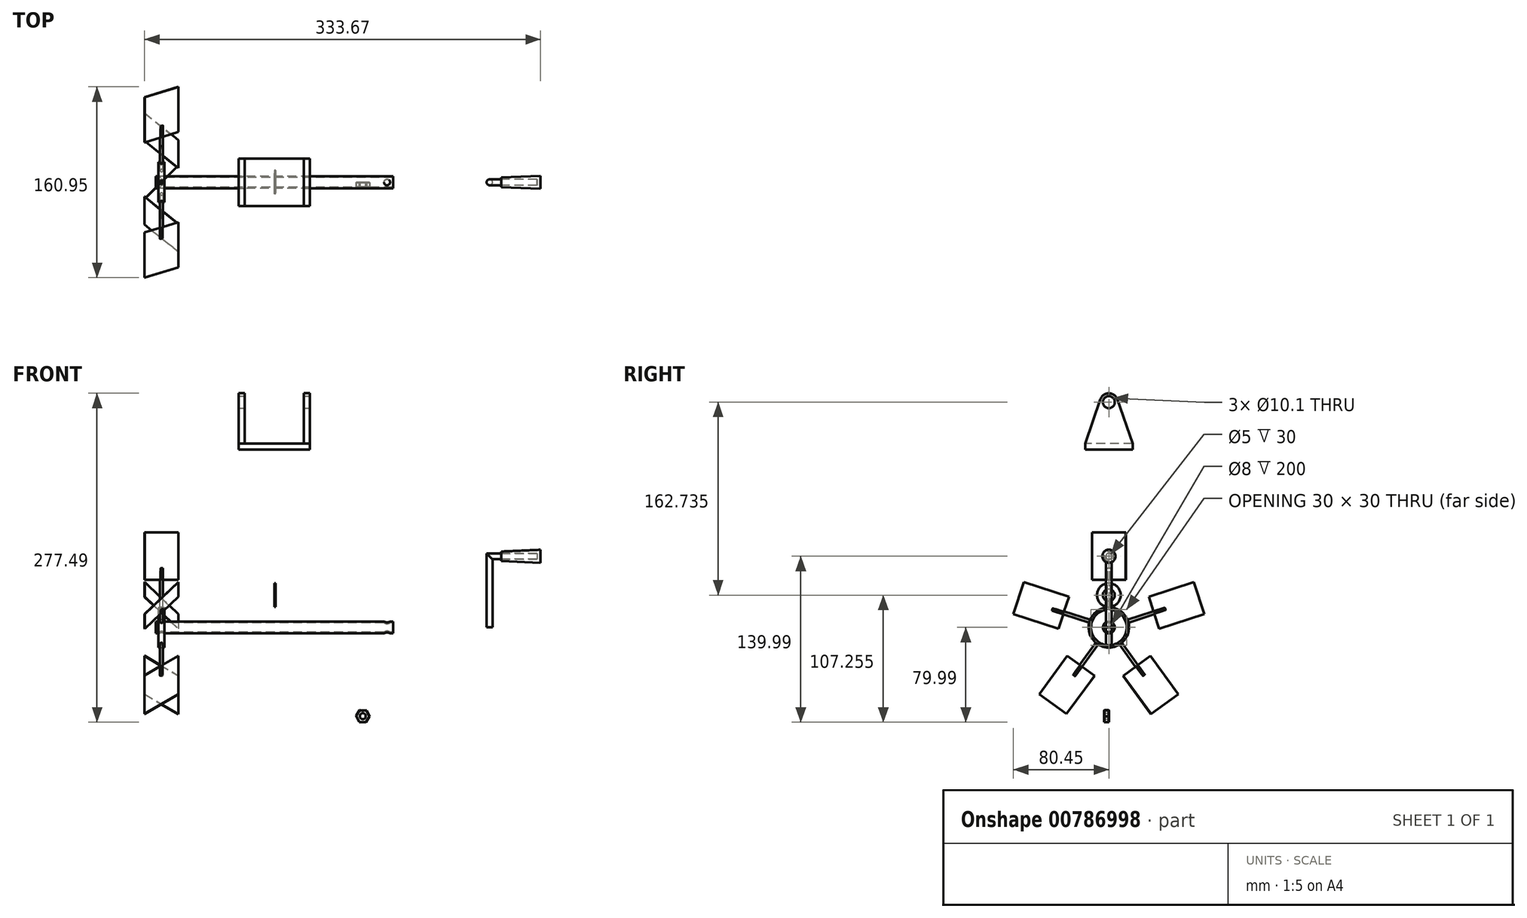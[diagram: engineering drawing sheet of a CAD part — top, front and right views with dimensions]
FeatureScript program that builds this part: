
annotation { "Feature Type Name" : "Feature", "Feature Type Description" : "" }
export const myFeature = defineFeature(function(context is Context, id is Id, definition is map)
    precondition{}
    {
        {
            var Q0;
            Q0=qCreatedBy(makeId("Front.planeOp"),FACE);
            var sketch = newSketch(context, id + "F0", { "sketchPlane" : qUnion([Q0])});
            skLineSegment(sketch, "E0.bottom", {"start": v(-100, 5) * mm, "end": v(100, 5) * mm});
            skLineSegment(sketch, "E0.top", {"start": v(-100, 4) * mm, "end": v(100, 4) * mm});
            skLineSegment(sketch, "E0.left", {"start": v(-100, 5) * mm, "end": v(-100, 4) * mm});
            skLineSegment(sketch, "E0.right", {"start": v(100, 5) * mm, "end": v(100, 4) * mm});
            skLineSegment(sketch, "E1", {"start": v(-144.44, 0) * mm, "end": v(183.91, 0) * mm, "construction": true});
            skSolve(sketch);
        }
        {
            var Q0;
            Q0 = qSketchRegion(id + "F0", true);
            var Q1;
            Q1=sQuery(id+"F0.wireOp",EDGE,"E1");
            revolve(context, id + "F1", {"surfaceOperationType" : NewSurfaceOperationType.NEW, "entities" : qUnion([Q0]), "axis" : qUnion([Q1]), "revolveType" : RevolveType.FULL});
        }
        {
            var Q0;
            Q0=qCreatedBy(makeId("Top.planeOp"),FACE);
            cPlane(context, id + "F2", {"entities" : qUnion([Q0]), "cplaneType" : CPlaneType.OFFSET, "offset" : 150 * mm, "width" : 150 * mm, "height" : 150 * mm});
        }
        {
            var Q0;
            Q0=qCreatedBy(id+"F2.planeOp",FACE);
            var sketch = newSketch(context, id + "F3", { "sketchPlane" : qUnion([Q0])});
            skLineSegment(sketch, "E2.bottom", {"start": v(25, 20) * mm, "end": v(-25, 20) * mm});
            skLineSegment(sketch, "E2.top", {"start": v(25, -20) * mm, "end": v(-25, -20) * mm});
            skLineSegment(sketch, "E2.left", {"start": v(25, 20) * mm, "end": v(25, -20) * mm});
            skLineSegment(sketch, "E2.right", {"start": v(-25, 20) * mm, "end": v(-25, -20) * mm});
            skPoint(sketch, "E2.middle", {"position": v(0, 0) * mm});
            skSolve(sketch);
        }
        {
            var Q0;
            Q0 = qSketchRegion(id + "F3", true);
            extrude(context, id + "F4", {"entities" : qUnion([Q0]), "depth" : 5 * mm, "offsetDistance" : 25 * mm});
        }
        {
            var Q0;
            Q0=makeQuery(id+"F4.opExtrude","SWEPT_FACE",FACE,{"disambiguationData":[OSD([sQuery(id+"F3.wireOp",EDGE,"E2.left")])]});
            cPlane(context, id + "F5", {"entities" : qUnion([Q0]), "cplaneType" : CPlaneType.OFFSET, "offset" : 5 * mm, "width" : 150 * mm, "height" : 150 * mm});
        }
        {
            var Q0;
            Q0=qCreatedBy(id+"F5.planeOp",FACE);
            var sketch = newSketch(context, id + "F6", { "sketchPlane" : qUnion([Q0])});
            skLineSegment(sketch, "E3.0", {"start": v(20, 150) * mm, "end": v(-20, 150) * mm});
            skLineSegment(sketch, "E4.0", {"start": v(-20, 155) * mm, "end": v(-20, 150) * mm});
            skLineSegment(sketch, "E5.0", {"start": v(20, 155) * mm, "end": v(20, 150) * mm});
            skCircle(sketch, "E6", {"center": v(0, 190) * mm, "radius": 5.05 * mm});
            skCircle(sketch, "E7", {"center": v(0, 190) * mm, "radius": 7.5 * mm});
            skLineSegment(sketch, "E8", {"start": v(-20, 155) * mm, "end": v(-7.1, 192.44) * mm});
            skLineSegment(sketch, "E9", {"start": v(20, 155) * mm, "end": v(7.1, 192.44) * mm});
            skSolve(sketch);
        }
        {
            var Q0;
            Q0 = qSketchRegion(id + "F6", true);
            extrude(context, id + "F7", {"entities" : qUnion([Q0]), "operationType" : NewBodyOperationType.ADD, "oppositeDirection" : true, "depth" : 5 * mm, "offsetDistance" : 25 * mm});
        }
        {
            var Q0;
            Q0=makeQuery(id+"F4.opExtrude","SWEPT_FACE",FACE,{"disambiguationData":[OSD([sQuery(id+"F3.wireOp",EDGE,"E2.right")])]});
            var sketch = newSketch(context, id + "F8", { "sketchPlane" : qUnion([Q0])});
            skLineSegment(sketch, "E10.0", {"start": v(20, 150) * mm, "end": v(-20, 150) * mm});
            skLineSegment(sketch, "E11.0", {"start": v(-20, 155) * mm, "end": v(-20, 150) * mm});
            skLineSegment(sketch, "E12.0", {"start": v(20, 155) * mm, "end": v(20, 150) * mm});
            skCircle(sketch, "E13", {"center": v(0, 190) * mm, "radius": 5.05 * mm});
            skCircle(sketch, "E14", {"center": v(0, 190) * mm, "radius": 7.5 * mm});
            skLineSegment(sketch, "E15", {"start": v(-20, 155) * mm, "end": v(-7.1, 192.44) * mm});
            skLineSegment(sketch, "E16", {"start": v(20, 155) * mm, "end": v(7.1, 192.44) * mm});
            skSolve(sketch);
        }
        {
            var Q0;
            Q0 = qSketchRegion(id + "F8", true);
            extrude(context, id + "F9", {"entities" : qUnion([Q0]), "operationType" : NewBodyOperationType.ADD, "depth" : 5 * mm, "offsetDistance" : 25 * mm});
        }
        {
            var Q0;
            Q0=qCreatedBy(makeId("Right.planeOp"),FACE);
            var sketch = newSketch(context, id + "F10", { "sketchPlane" : qUnion([Q0])});
            skCircle(sketch, "E17", {"center": v(0, 27.26) * mm, "radius": 5.05 * mm});
            skCircle(sketch, "E18", {"center": v(0, 27.26) * mm, "radius": 10 * mm});
            skSolve(sketch);
        }
        {
            var Q0;
            Q0=makeQuery(id+"F10.imprint","IMPRINT",FACE,{"disambiguationData":[TD([[makeQuery(id+"F10.imprint","IMPRINT",EDGE,{"derivedFrom":sQuery(id+"F10.wireOp",EDGE,"E17")}),-1.0]])]});
            extrude(context, id + "F11", {"entities" : qUnion([Q0]), "depth" : 1 * mm, "offsetDistance" : 25 * mm});
        }
        {
            var Q0;
            Q0=qCreatedBy(makeId("Front.planeOp"),FACE);
            var sketch = newSketch(context, id + "F12", { "sketchPlane" : qUnion([Q0])});
            skLineSegment(sketch, "E19", {"start": v(-100, 5) * mm, "end": v(100, 5) * mm, "construction": true});
            skSolve(sketch);
        }
        {
            var Q0;
            Q0=sQuery(id+"F12.wireOp",EDGE,"E19");
            cPlane(context, id + "F13", {"entities" : qUnion([Q0]), "cplaneType" : CPlaneType.LINE_ANGLE, "offset" : 25 * mm, "angle" : 90 * degree, "width" : 150 * mm, "height" : 150 * mm});
        }
        {
            var Q0;
            Q0=qCreatedBy(id+"F13.planeOp",FACE);
            var sketch = newSketch(context, id + "F14", { "sketchPlane" : qUnion([Q0])});
            skCircle(sketch, "E20", {"center": v(95, 0) * mm, "radius": 2.55 * mm});
            skSolve(sketch);
        }
        {
            var Q0;
            Q0=makeQuery(id+"F14.imprint","IMPRINT",FACE,{"disambiguationData":[TD([[makeQuery(id+"F14.imprint","IMPRINT",EDGE,{"derivedFrom":sQuery(id+"F14.wireOp",EDGE,"E20")}),1.0]])]});
            extrude(context, id + "F15", {"entities" : qUnion([Q0]), "operationType" : NewBodyOperationType.REMOVE, "oppositeDirection" : true, "depth" : 25 * mm, "offsetDistance" : 25 * mm});
        }
        {
            var Q0;
            Q0=qCreatedBy(makeId("Front.planeOp"),FACE);
            var sketch = newSketch(context, id + "F16", { "sketchPlane" : qUnion([Q0])});
            skLineSegment(sketch, "E21", {"start": v(181.39, 0) * mm, "end": v(181.39, 60) * mm});
            skLineSegment(sketch, "E22", {"start": v(181.39, 60) * mm, "end": v(221.39, 60) * mm});
            skSolve(sketch);
        }
        {
            var Q0;
            Q0=qCreatedBy(makeId("Top.planeOp"),FACE);
            var sketch = newSketch(context, id + "F17", { "sketchPlane" : qUnion([Q0])});
            skPoint(sketch, "E23.0", {"position": v(181.39, 0) * mm});
            skCircle(sketch, "E24", {"center": v(181.39, 0) * mm, "radius": 2.5 * mm});
            skSolve(sketch);
        }
        {
            var Q0;
            Q0=makeQuery(id+"F17.imprint","IMPRINT",FACE,{"disambiguationData":[TD([[makeQuery(id+"F17.imprint","IMPRINT",EDGE,{"derivedFrom":sQuery(id+"F17.wireOp",EDGE,"E24")}),1.0]])]});
            var Q1;
            Q1=sQuery(id+"F16.wireOp",EDGE,"E21");
            var Q2;
            Q2=sQuery(id+"F16.wireOp",EDGE,"E22");
            sweep(context, id + "F18", {"profiles" : qUnion([Q0]), "path" : qUnion([Q1, Q2])});
        }
        {
            var Q0;
            Q0=sQuery(id+"F16.wireOp",EDGE,"E22");
            cPlane(context, id + "F19", {"entities" : qUnion([Q0]), "cplaneType" : CPlaneType.LINE_ANGLE, "offset" : 25 * mm, "angle" : 270 * degree, "width" : 150 * mm, "height" : 150 * mm});
        }
        {
            var Q0;
            Q0=qCreatedBy(id+"F19.planeOp",FACE);
            var sketch = newSketch(context, id + "F20", { "sketchPlane" : qUnion([Q0])});
            skLineSegment(sketch, "E25.0", {"start": v(181.39, 0) * mm, "end": v(221.39, 0) * mm});
            skLineSegment(sketch, "E26", {"start": v(224.39, 0) * mm, "end": v(224.39, 5.5) * mm});
            skLineSegment(sketch, "E27", {"start": v(224.39, 5.5) * mm, "end": v(191.39, 4) * mm});
            skLineSegment(sketch, "E28", {"start": v(191.39, 4) * mm, "end": v(191.39, 2.5) * mm});
            skLineSegment(sketch, "E29", {"start": v(191.39, 2.5) * mm, "end": v(221.39, 2.5) * mm});
            skLineSegment(sketch, "E30", {"start": v(221.39, 2.5) * mm, "end": v(221.39, 0) * mm});
            skLineSegment(sketch, "E31", {"start": v(221.39, 0) * mm, "end": v(224.39, 0) * mm});
            skSolve(sketch);
        }
        {
            var Q0;
            Q0=makeQuery(id+"F20.imprint","IMPRINT",FACE,{"disambiguationData":[TD([[makeQuery(id+"F20.imprint","IMPRINT",EDGE,{"derivedFrom":sQuery(id+"F20.wireOp",EDGE,"E26")}),1.0]])]});
            var Q1;
            Q1=sQuery(id+"F20.wireOp",EDGE,"E25.0");
            revolve(context, id + "F21", {"surfaceOperationType" : NewSurfaceOperationType.NEW, "entities" : qUnion([Q0]), "axis" : qUnion([Q1]), "revolveType" : RevolveType.FULL});
        }
        {
            var Q0;
            Q0=qCreatedBy(makeId("Right.planeOp"),FACE);
            cPlane(context, id + "F22", {"entities" : qUnion([Q0]), "cplaneType" : CPlaneType.OFFSET, "offset" : 95 * mm, "oppositeDirection" : true, "width" : 150 * mm, "height" : 150 * mm});
        }
        {
            var Q0;
            Q0=qCreatedBy(id+"F22.planeOp",FACE);
            var sketch = newSketch(context, id + "F23", { "sketchPlane" : qUnion([Q0])});
            skCircle(sketch, "E32", {"center": v(0, 0) * mm, "radius": 15 * mm});
            skCircle(sketch, "E33", {"center": v(0, 0) * mm, "radius": 17 * mm});
            skCircle(sketch, "E34", {"center": v(0, 0) * mm, "radius": 50 * mm, "construction": true});
            skPoint(sketch, "E35", {"position": v(0, 50) * mm});
            skSolve(sketch);
        }
        {
            var Q0;
            Q0 = qSketchRegion(id + "F23", true);
            extrude(context, id + "F24", {"entities" : qUnion([Q0]), "endBound" : BoundingType.SYMMETRIC, "oppositeDirection" : true, "depth" : 5 * mm, "offsetDistance" : 25 * mm});
        }
        {
            var Q0;
            Q0=qCreatedBy(makeId("Top.planeOp"),FACE);
            var sketch = newSketch(context, id + "F25", { "sketchPlane" : qUnion([Q0])});
            skCircle(sketch, "E36", {"center": v(-95, 0) * mm, "radius": 2.5 * mm});
            skSolve(sketch);
        }
        {
            var Q0;
            Q0 = qSketchRegion(id + "F25", true);
            extrude(context, id + "F26", {"entities" : qUnion([Q0]), "operationType" : NewBodyOperationType.ADD, "endBound" : BoundingType.SYMMETRIC, "depth" : 30 * mm, "offsetDistance" : 25 * mm});
        }
        {
            var Q0;
            Q0=sQuery(id+"F23.wireOp",VERTEX,"E35");
            var Q1;
            Q1=qCreatedBy(makeId("Top.planeOp"),FACE);
            cPlane(context, id + "F27", {"entities" : qUnion([Q0, Q1]), "cplaneType" : CPlaneType.PLANE_POINT, "offset" : 25 * mm, "width" : 150 * mm, "height" : 150 * mm});
        }
        {
            var Q0;
            Q0=qCreatedBy(id+"F27.planeOp",FACE);
            var sketch = newSketch(context, id + "F28", { "sketchPlane" : qUnion([Q0])});
            skPoint(sketch, "E37.0", {"position": v(-95, 0) * mm});
            skCircle(sketch, "E38", {"center": v(-95, 0) * mm, "radius": 1.25 * mm});
            skSolve(sketch);
        }
        {
            var Q0;
            Q0 = qSketchRegion(id + "F28", true);
            var Q1;
            Q1=makeQuery(id+"F24.opExtrude","SWEPT_FACE",FACE,{"disambiguationData":[OSD([sQuery(id+"F23.wireOp",EDGE,"E33")])]});
            extrude(context, id + "F29", {"entities" : qUnion([Q0]), "endBound" : BoundingType.UP_TO_SURFACE, "oppositeDirection" : true, "depth" : 25 * mm, "endBoundEntityFace" : qUnion([Q1]), "offsetDistance" : 25 * mm});
        }
        {
            var Q0;
            Q0=makeQuery(id+"F28.imprint","IMPRINT",FACE,{"disambiguationData":[TD([[makeQuery(id+"F28.imprint","IMPRINT",EDGE,{"derivedFrom":sQuery(id+"F28.wireOp",EDGE,"E38")}),1.0]])]});
            var sketch = newSketch(context, id + "F30", { "sketchPlane" : qUnion([Q0])});
            skPoint(sketch, "E39.0", {"position": v(-95, 0) * mm});
            skLineSegment(sketch, "E40", {"start": v(-95, 2.52) * mm, "end": v(-95, -2.49) * mm, "construction": true});
            skCircle(sketch, "E41.0", {"center": v(-95, 0) * mm, "radius": 1.25 * mm});
            skLineSegment(sketch, "E42", {"start": v(-94.27, 1.01) * mm, "end": v(-96.01, -0.73) * mm});
            skLineSegment(sketch, "E43", {"start": v(-95.73, -1.01) * mm, "end": v(-93.99, 0.73) * mm});
            skSolve(sketch);
        }
        {
            var Q0;
            {var subQ0=sQuery(id+"F30.wireOp",EDGE,"E42");Q0=makeQuery(id+"F30.imprint","IMPRINT",FACE,{"disambiguationData":[TD([[makeQuery(id+"F30.imprint","IMPRINT",EDGE,{"derivedFrom":subQ0}),1.0]])]});}
            extrude(context, id + "F31", {"entities" : qUnion([Q0]), "operationType" : NewBodyOperationType.REMOVE, "oppositeDirection" : true, "depth" : 10 * mm, "offsetDistance" : 25 * mm});
        }
        {
            var Q0;
            Q0=makeQuery(id+"F31.boolean.opBoolean","COPY",FACE,{"derivedFrom":makeQuery(id+"F31.opExtrude","SWEPT_FACE",FACE,{"disambiguationData":[OSD([sQuery(id+"F30.wireOp",EDGE,"E42")])]})});
            var sketch = newSketch(context, id + "F32", { "sketchPlane" : qUnion([Q0])});
            skPoint(sketch, "E44.0", {"position": v(-67.18, 50) * mm});
            skLineSegment(sketch, "E45.bottom", {"start": v(-87.18, 80) * mm, "end": v(-47.18, 80) * mm});
            skLineSegment(sketch, "E45.top", {"start": v(-87.18, 40) * mm, "end": v(-47.18, 40) * mm});
            skLineSegment(sketch, "E45.left", {"start": v(-87.18, 80) * mm, "end": v(-87.18, 40) * mm});
            skLineSegment(sketch, "E45.right", {"start": v(-47.18, 80) * mm, "end": v(-47.18, 40) * mm});
            skSolve(sketch);
        }
        {
            var Q0;
            Q0 = qSketchRegion(id + "F32", true);
            extrude(context, id + "F33", {"entities" : qUnion([Q0]), "depth" : 0.2 * mm, "offsetDistance" : 25 * mm});
        }
        {
            var Q0;
            Q0=makeQuery(id+"F29.opExtrude","SWEPT_BODY",BODY,{"disambiguationData":[OSD([sQuery(id+"F28.wireOp",EDGE,"E38")])]});
            var Q1;
            Q1=makeQuery(id+"F33.opExtrude","SWEPT_BODY",BODY,{"disambiguationData":[OSD([sQuery(id+"F32.wireOp",EDGE,"E45.bottom"),sQuery(id+"F32.wireOp",EDGE,"E45.top"),sQuery(id+"F32.wireOp",EDGE,"E45.left"),sQuery(id+"F32.wireOp",EDGE,"E45.right")])]});
            var Q2;
            Q2=sQuery(id+"F23.wireOp",EDGE,"E33");
            circularPattern(context, id + "F34", {"entities" : qUnion([Q0, Q1]), "axis" : qUnion([Q2]), "angle" : 360 * degree, "instanceCount" : 5, "equalSpace" : true});
        }
        {
            var Q0;
            Q0=qCreatedBy(makeId("Front.planeOp"),FACE);
            var sketch = newSketch(context, id + "F35", { "sketchPlane" : qUnion([Q0])});
            skCircle(sketch, "E46.cCircle", {"center": v(74.6, -74.87) * mm, "radius": 5 * mm, "construction": true});
            skLineSegment(sketch, "E46.0", {"start": v(68.82, -74.6) * mm, "end": v(71.94, -69.74) * mm});
            skLineSegment(sketch, "E46.1", {"start": v(71.94, -69.74) * mm, "end": v(77.7, -70) * mm});
            skLineSegment(sketch, "E46.2", {"start": v(77.7, -70) * mm, "end": v(80.36, -75.14) * mm});
            skLineSegment(sketch, "E46.3", {"start": v(80.36, -75.14) * mm, "end": v(77.24, -80) * mm});
            skLineSegment(sketch, "E46.4", {"start": v(77.24, -80) * mm, "end": v(71.48, -79.73) * mm});
            skLineSegment(sketch, "E46.5", {"start": v(71.48, -79.73) * mm, "end": v(68.82, -74.6) * mm});
            skPoint(sketch, "E46.0.midPoint", {"position": v(70.38, -72.17) * mm});
            skCircle(sketch, "E47", {"center": v(74.6, -74.87) * mm, "radius": 2.5 * mm});
            skSolve(sketch);
        }
        {
            var Q0;
            Q0=makeQuery(id+"F35.imprint","IMPRINT",FACE,{"disambiguationData":[TD([[makeQuery(id+"F35.imprint","IMPRINT",EDGE,{"derivedFrom":sQuery(id+"F35.wireOp",EDGE,"E46.0")}),-1.0]])]});
            extrude(context, id + "F36", {"entities" : qUnion([Q0]), "depth" : 4 * mm, "offsetDistance" : 25 * mm});
        }
        {
            var Q0;
            Q0=makeQuery(id+"F36.opExtrude","SWEPT_EDGE",EDGE,{"disambiguationData":[OSD([sQuery(id+"F35.wireOp",EDGE,"E46.0"),sQuery(id+"F35.wireOp",EDGE,"E46.5")])]});
            var Q1;
            Q1=makeQuery(id+"F36.opExtrude","CAP_EDGE",EDGE,{"disambiguationData":[OSD([sQuery(id+"F35.wireOp",EDGE,"E46.0")])],"isStart":false});
            var Q2;
            Q2=makeQuery(id+"F36.opExtrude","CAP_EDGE",EDGE,{"disambiguationData":[OSD([sQuery(id+"F35.wireOp",EDGE,"E46.5")])],"isStart":false});
            var Q3;
            Q3=makeQuery(id+"F36.opExtrude","CAP_EDGE",EDGE,{"disambiguationData":[OSD([sQuery(id+"F35.wireOp",EDGE,"E46.1")])],"isStart":false});
            var Q4;
            Q4=makeQuery(id+"F36.opExtrude","CAP_EDGE",EDGE,{"disambiguationData":[OSD([sQuery(id+"F35.wireOp",EDGE,"E46.2")])],"isStart":false});
            var Q5;
            Q5=makeQuery(id+"F36.opExtrude","CAP_EDGE",EDGE,{"disambiguationData":[OSD([sQuery(id+"F35.wireOp",EDGE,"E46.3")])],"isStart":false});
            var Q6;
            Q6=makeQuery(id+"F36.opExtrude","CAP_EDGE",EDGE,{"disambiguationData":[OSD([sQuery(id+"F35.wireOp",EDGE,"E46.4")])],"isStart":false});
            var Q7;
            Q7=makeQuery(id+"F36.opExtrude","SWEPT_EDGE",EDGE,{"disambiguationData":[OSD([sQuery(id+"F35.wireOp",EDGE,"E46.4"),sQuery(id+"F35.wireOp",EDGE,"E46.5")])]});
            var Q8;
            Q8=makeQuery(id+"F36.opExtrude","SWEPT_EDGE",EDGE,{"disambiguationData":[OSD([sQuery(id+"F35.wireOp",EDGE,"E46.3"),sQuery(id+"F35.wireOp",EDGE,"E46.4")])]});
            var Q9;
            Q9=makeQuery(id+"F36.opExtrude","SWEPT_EDGE",EDGE,{"disambiguationData":[OSD([sQuery(id+"F35.wireOp",EDGE,"E46.2"),sQuery(id+"F35.wireOp",EDGE,"E46.3")])]});
            var Q10;
            Q10=makeQuery(id+"F36.opExtrude","SWEPT_EDGE",EDGE,{"disambiguationData":[OSD([sQuery(id+"F35.wireOp",EDGE,"E46.1"),sQuery(id+"F35.wireOp",EDGE,"E46.2")])]});
            var Q11;
            Q11=makeQuery(id+"F36.opExtrude","SWEPT_EDGE",EDGE,{"disambiguationData":[OSD([sQuery(id+"F35.wireOp",EDGE,"E46.0"),sQuery(id+"F35.wireOp",EDGE,"E46.1")])]});
            var Q12;
            Q12=makeQuery(id+"F36.opExtrude","CAP_EDGE",EDGE,{"disambiguationData":[OSD([sQuery(id+"F35.wireOp",EDGE,"E46.0")])],"isStart":true});
            var Q13;
            Q13=makeQuery(id+"F36.opExtrude","CAP_EDGE",EDGE,{"disambiguationData":[OSD([sQuery(id+"F35.wireOp",EDGE,"E46.1")])],"isStart":true});
            var Q14;
            Q14=makeQuery(id+"F36.opExtrude","CAP_EDGE",EDGE,{"disambiguationData":[OSD([sQuery(id+"F35.wireOp",EDGE,"E46.2")])],"isStart":true});
            var Q15;
            Q15=makeQuery(id+"F36.opExtrude","CAP_EDGE",EDGE,{"disambiguationData":[OSD([sQuery(id+"F35.wireOp",EDGE,"E46.3")])],"isStart":true});
            var Q16;
            Q16=makeQuery(id+"F36.opExtrude","CAP_EDGE",EDGE,{"disambiguationData":[OSD([sQuery(id+"F35.wireOp",EDGE,"E46.4")])],"isStart":true});
            var Q17;
            Q17=makeQuery(id+"F36.opExtrude","CAP_EDGE",EDGE,{"disambiguationData":[OSD([sQuery(id+"F35.wireOp",EDGE,"E46.5")])],"isStart":true});
            chamfer(context, id + "F37", {"entities" : qUnion([Q0, Q1, Q2, Q3, Q4, Q5, Q6, Q7, Q8, Q9, Q10, Q11, Q12, Q13, Q14, Q15, Q16, Q17]), "width" : 0.2 * mm, "tangentPropagation" : true});
        }
    });
